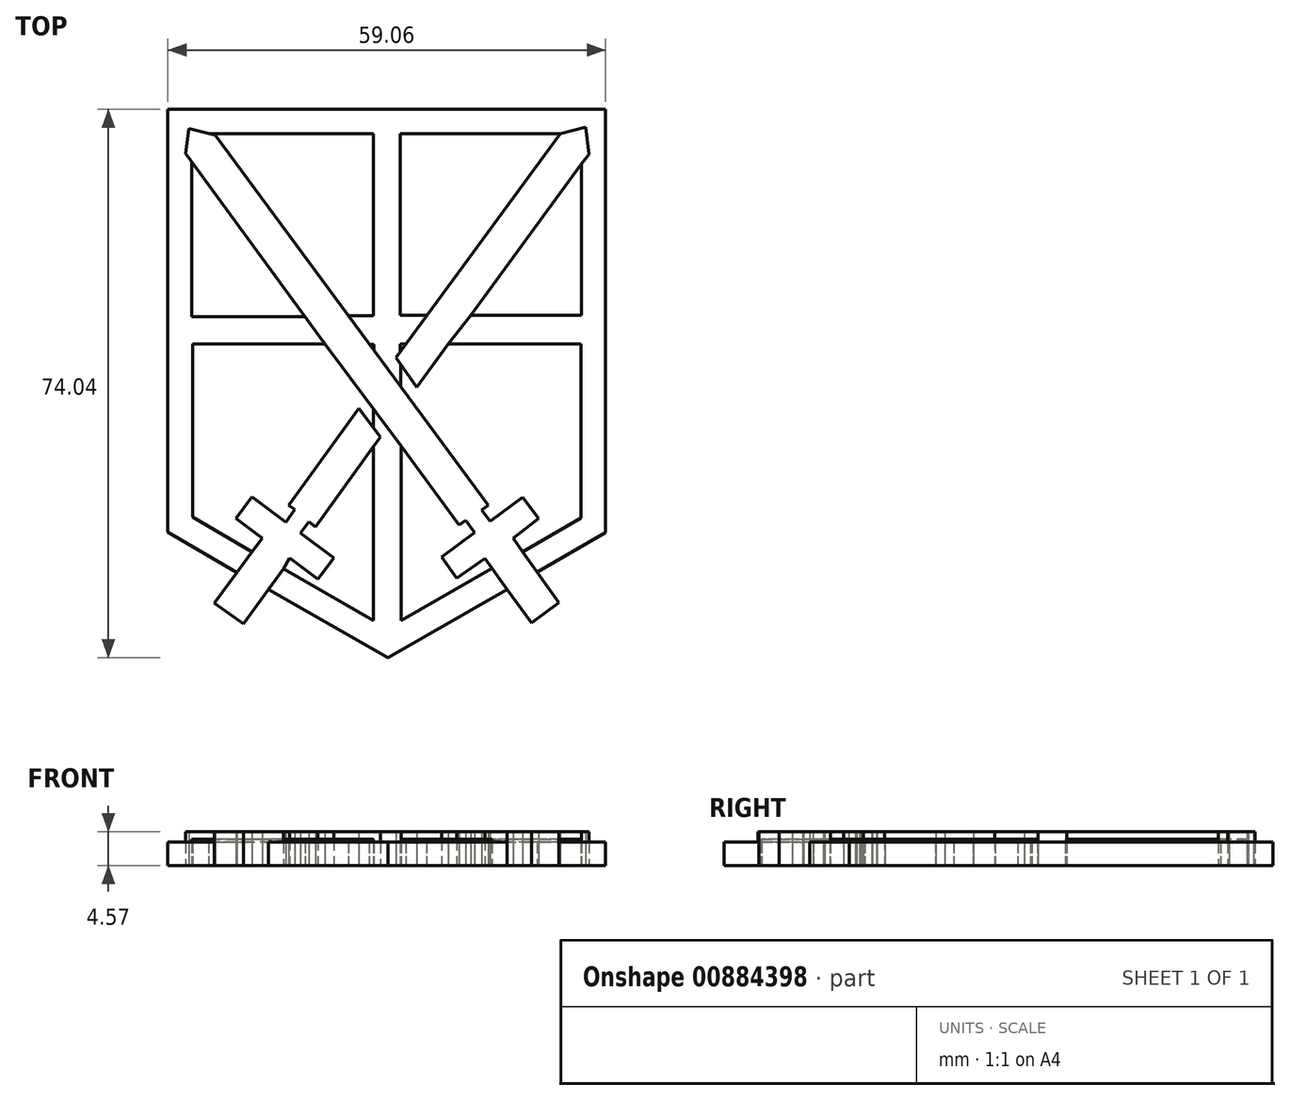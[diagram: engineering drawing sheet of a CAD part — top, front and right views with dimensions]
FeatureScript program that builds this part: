
annotation { "Feature Type Name" : "Feature", "Feature Type Description" : "" }
export const myFeature = defineFeature(function(context is Context, id is Id, definition is map)
    precondition{}
    {
        {
            var Q0;
            Q0=qCreatedBy(makeId("Top.planeOp"),FACE);
            var sketch = newSketch(context, id + "F0", { "sketchPlane" : qUnion([Q0])});
            skLineSegment(sketch, "E0", {"start": v(29.58, 29.95) * mm, "end": v(29.58, -27.22) * mm});
            skLineSegment(sketch, "E1", {"start": v(29.58, -27.22) * mm, "end": v(20.36, -32.55) * mm});
            skLineSegment(sketch, "E2", {"start": v(20.36, -32.55) * mm, "end": v(18.4, -29.78) * mm});
            skLineSegment(sketch, "E3", {"start": v(18.4, -29.78) * mm, "end": v(17.1, -28) * mm});
            skLineSegment(sketch, "E4", {"start": v(20.36, -32.55) * mm, "end": v(23.28, -36.68) * mm});
            skLineSegment(sketch, "E5", {"start": v(23.28, -36.68) * mm, "end": v(19.6, -39.39) * mm});
            skLineSegment(sketch, "E6", {"start": v(19.6, -39.39) * mm, "end": v(16.3, -34.9) * mm});
            skLineSegment(sketch, "E7", {"start": v(16.3, -34.9) * mm, "end": v(14.28, -32.03) * mm});
            skLineSegment(sketch, "E8", {"start": v(14.28, -32.03) * mm, "end": v(13.32, -30.68) * mm});
            skLineSegment(sketch, "E9", {"start": v(16.3, -34.9) * mm, "end": v(0.2, -44.09) * mm});
            skLineSegment(sketch, "E10", {"start": v(0.2, -44.09) * mm, "end": v(-15.92, -34.9) * mm});
            skLineSegment(sketch, "E11", {"start": v(-15.92, -34.9) * mm, "end": v(-19.28, -39.55) * mm});
            skLineSegment(sketch, "E12", {"start": v(-19.28, -39.55) * mm, "end": v(-23.19, -36.72) * mm});
            skLineSegment(sketch, "E13", {"start": v(-23.19, -36.72) * mm, "end": v(-20.19, -32.58) * mm});
            skLineSegment(sketch, "E14", {"start": v(-20.19, -32.58) * mm, "end": v(-18.12, -29.83) * mm});
            skLineSegment(sketch, "E15", {"start": v(-18.12, -29.83) * mm, "end": v(-16.72, -27.98) * mm});
            skLineSegment(sketch, "E16", {"start": v(-16.72, -27.98) * mm, "end": v(-20.3, -25.28) * mm});
            skLineSegment(sketch, "E17", {"start": v(-20.3, -25.28) * mm, "end": v(-18.12, -22.4) * mm});
            skLineSegment(sketch, "E18", {"start": v(-15.92, -34.9) * mm, "end": v(-13.9, -32.13) * mm});
            skLineSegment(sketch, "E19", {"start": v(-13.9, -32.13) * mm, "end": v(-13.05, -30.63) * mm});
            skLineSegment(sketch, "E20", {"start": v(-13.05, -30.63) * mm, "end": v(-9.23, -33.5) * mm});
            skLineSegment(sketch, "E21", {"start": v(-9.23, -33.5) * mm, "end": v(-7.07, -30.63) * mm});
            skLineSegment(sketch, "E22", {"start": v(-13.9, -32.13) * mm, "end": v(-1.74, -39.06) * mm});
            skLineSegment(sketch, "E23", {"start": v(-1.74, -39.06) * mm, "end": v(-1.74, -15.6) * mm});
            skLineSegment(sketch, "E24", {"start": v(13.32, -30.68) * mm, "end": v(9.49, -33.4) * mm});
            skLineSegment(sketch, "E25", {"start": v(9.49, -33.4) * mm, "end": v(7.45, -30.51) * mm});
            skLineSegment(sketch, "E26", {"start": v(7.45, -30.51) * mm, "end": v(18.41, -22.43) * mm});
            skLineSegment(sketch, "E27", {"start": v(18.41, -22.43) * mm, "end": v(20.53, -25.3) * mm});
            skLineSegment(sketch, "E28", {"start": v(20.53, -25.3) * mm, "end": v(17.1, -28) * mm});
            skLineSegment(sketch, "E29", {"start": v(-7.07, -30.63) * mm, "end": v(-18.12, -22.4) * mm});
            skLineSegment(sketch, "E30", {"start": v(2.02, -15.53) * mm, "end": v(2.02, -39.07) * mm});
            skLineSegment(sketch, "E31", {"start": v(2.02, -39.07) * mm, "end": v(14.28, -32.03) * mm});
            skLineSegment(sketch, "E32", {"start": v(18.4, -29.78) * mm, "end": v(26.27, -25.2) * mm});
            skLineSegment(sketch, "E33", {"start": v(26.27, -25.2) * mm, "end": v(26.27, -1.77) * mm});
            skLineSegment(sketch, "E34", {"start": v(26.27, -1.77) * mm, "end": v(8.38, -1.77) * mm});
            skLineSegment(sketch, "E35", {"start": v(8.38, -1.77) * mm, "end": v(11.37, 2.12) * mm});
            skLineSegment(sketch, "E36", {"start": v(11.37, 2.12) * mm, "end": v(26.33, 2.12) * mm});
            skLineSegment(sketch, "E37", {"start": v(26.33, 2.12) * mm, "end": v(26.33, 22.57) * mm});
            skLineSegment(sketch, "E38", {"start": v(26.33, 22.57) * mm, "end": v(27.34, 23.84) * mm});
            skLineSegment(sketch, "E39", {"start": v(27.34, 23.84) * mm, "end": v(26.92, 27.54) * mm});
            skLineSegment(sketch, "E40", {"start": v(26.92, 27.54) * mm, "end": v(23.46, 26.65) * mm});
            skLineSegment(sketch, "E41", {"start": v(23.46, 26.65) * mm, "end": v(1.27, -3.57) * mm});
            skLineSegment(sketch, "E42", {"start": v(1.27, -3.57) * mm, "end": v(4.1, -7.57) * mm});
            skLineSegment(sketch, "E43", {"start": v(4.1, -7.57) * mm, "end": v(8.38, -1.77) * mm});
            skLineSegment(sketch, "E44", {"start": v(11.37, 2.12) * mm, "end": v(26.33, 22.57) * mm});
            skLineSegment(sketch, "E45", {"start": v(23.46, 26.65) * mm, "end": v(1.9, 26.65) * mm});
            skLineSegment(sketch, "E46", {"start": v(1.9, 26.65) * mm, "end": v(1.9, 2.12) * mm});
            skLineSegment(sketch, "E47", {"start": v(1.9, 2.12) * mm, "end": v(5.45, 2.12) * mm});
            skLineSegment(sketch, "E48", {"start": v(29.58, 29.95) * mm, "end": v(-29.48, 29.95) * mm});
            skLineSegment(sketch, "E49", {"start": v(-29.48, 29.95) * mm, "end": v(-29.48, -27.13) * mm});
            skLineSegment(sketch, "E50", {"start": v(-29.48, -27.13) * mm, "end": v(-20.19, -32.58) * mm});
            skLineSegment(sketch, "E51", {"start": v(-18.12, -29.83) * mm, "end": v(-26.13, -25.13) * mm});
            skLineSegment(sketch, "E52", {"start": v(-26.13, -25.13) * mm, "end": v(-26.13, -1.77) * mm});
            skLineSegment(sketch, "E53", {"start": v(-26.13, -1.77) * mm, "end": v(-8.27, -1.77) * mm});
            skLineSegment(sketch, "E54", {"start": v(-8.27, -1.77) * mm, "end": v(2.02, -15.53) * mm});
            skLineSegment(sketch, "E55", {"start": v(2.02, -15.53) * mm, "end": v(9.8, -26.18) * mm});
            skLineSegment(sketch, "E56", {"start": v(9.8, -26.18) * mm, "end": v(10.67, -25.54) * mm});
            skLineSegment(sketch, "E57", {"start": v(10.67, -25.54) * mm, "end": v(11.9, -27.23) * mm});
            skLineSegment(sketch, "E58", {"start": v(14, -25.68) * mm, "end": v(12.87, -24.15) * mm});
            skLineSegment(sketch, "E59", {"start": v(12.87, -24.15) * mm, "end": v(13.74, -23.51) * mm});
            skLineSegment(sketch, "E60", {"start": v(13.74, -23.51) * mm, "end": v(-23.1, 26.43) * mm});
            skLineSegment(sketch, "E61", {"start": v(-23.1, 26.43) * mm, "end": v(-26.62, 27.36) * mm});
            skLineSegment(sketch, "E62", {"start": v(-26.62, 27.36) * mm, "end": v(-27.07, 24) * mm});
            skLineSegment(sketch, "E63", {"start": v(-27.07, 24) * mm, "end": v(-8.27, -1.77) * mm});
            skLineSegment(sketch, "E64", {"start": v(-10.97, 1.92) * mm, "end": v(-26.24, 1.92) * mm});
            skLineSegment(sketch, "E65", {"start": v(-26.24, 1.92) * mm, "end": v(-26.24, 22.87) * mm});
            skLineSegment(sketch, "E66", {"start": v(-1.76, 26.65) * mm, "end": v(-23.96, 26.65) * mm});
            skLineSegment(sketch, "E67", {"start": v(-1.76, 26.65) * mm, "end": v(-1.76, 2.04) * mm});
            skLineSegment(sketch, "E68", {"start": v(-1.76, 2.04) * mm, "end": v(-5.1, 2.04) * mm});
            skLineSegment(sketch, "E69", {"start": v(-1.7, -2.6) * mm, "end": v(-1.7, -1.8) * mm});
            skLineSegment(sketch, "E70", {"start": v(-1.7, -1.8) * mm, "end": v(-2.28, -1.8) * mm});
            skLineSegment(sketch, "E71", {"start": v(1.84, -2.79) * mm, "end": v(1.84, -1.74) * mm});
            skLineSegment(sketch, "E72", {"start": v(1.84, -1.74) * mm, "end": v(2.61, -1.74) * mm});
            skLineSegment(sketch, "E73", {"start": v(1.94, -7.52) * mm, "end": v(1.94, -4.51) * mm});
            skLineSegment(sketch, "E74", {"start": v(-1.72, -10.53) * mm, "end": v(-1.72, -13.1) * mm});
            skLineSegment(sketch, "E75", {"start": v(-1.72, -13.1) * mm, "end": v(-0.81, -14.32) * mm});
            skLineSegment(sketch, "E76", {"start": v(-0.81, -14.32) * mm, "end": v(-1.74, -15.6) * mm});
            skLineSegment(sketch, "E77", {"start": v(-1.72, -13.1) * mm, "end": v(-3.7, -10.45) * mm});
            skLineSegment(sketch, "E78", {"start": v(-3.7, -10.45) * mm, "end": v(-13.16, -23.5) * mm});
            skLineSegment(sketch, "E79", {"start": v(-13.16, -23.5) * mm, "end": v(-12.33, -24.1) * mm});
            skLineSegment(sketch, "E80", {"start": v(-12.33, -24.1) * mm, "end": v(-13.56, -25.8) * mm});
            skLineSegment(sketch, "E81", {"start": v(-11.57, -27.27) * mm, "end": v(-10.45, -25.76) * mm});
            skLineSegment(sketch, "E82", {"start": v(-10.45, -25.76) * mm, "end": v(-9.57, -26.42) * mm});
            skLineSegment(sketch, "E83", {"start": v(-9.57, -26.42) * mm, "end": v(-1.74, -15.6) * mm});
            skSolve(sketch);
        }
        {
            var Q0;
            Q0=makeQuery(id+"F0.imprint","IMPRINT",FACE,{"disambiguationData":[TD([[makeQuery(id+"F0.imprint","IMPRINT",EDGE,{"derivedFrom":sQuery(id+"F0.wireOp",EDGE,"E0")}),-1.0]])]});
            var Q1;
            Q1=makeQuery(id+"F0.imprint","IMPRINT",FACE,{"disambiguationData":[TD([[makeQuery(id+"F0.imprint","IMPRINT",EDGE,{"derivedFrom":sQuery(id+"F0.wireOp",EDGE,"E7")}),1.0]])]});
            extrude(context, id + "F1", {"entities" : qUnion([Q0, Q1]), "depth" : 3.17 * mm, "offsetDistance" : 25.4 * mm});
        }
        {
            var Q0;
            Q0=makeQuery(id+"F0.imprint","IMPRINT",FACE,{"disambiguationData":[TD([[makeQuery(id+"F0.imprint","IMPRINT",EDGE,{"derivedFrom":sQuery(id+"F0.wireOp",EDGE,"E15")}),1.0]])]});
            var Q1;
            {var subQ0=sQuery(id+"F0.wireOp",EDGE,"E64");Q1=makeQuery(id+"F0.imprint","IMPRINT",FACE,{"disambiguationData":[TD([[makeQuery(id+"F0.imprint","IMPRINT",EDGE,{"derivedFrom":subQ0}),-1.0]])]});}
            var Q2;
            {var subQ0=sQuery(id+"F0.wireOp",EDGE,"E66");Q2=makeQuery(id+"F0.imprint","IMPRINT",FACE,{"disambiguationData":[TD([[makeQuery(id+"F0.imprint","IMPRINT",EDGE,{"derivedFrom":subQ0}),1.0]])]});}
            var Q3;
            {var subQ0=sQuery(id+"F0.wireOp",EDGE,"E45");Q3=makeQuery(id+"F0.imprint","IMPRINT",FACE,{"disambiguationData":[TD([[makeQuery(id+"F0.imprint","IMPRINT",EDGE,{"derivedFrom":subQ0}),1.0]])]});}
            var Q4;
            Q4=makeQuery(id+"F0.imprint","IMPRINT",FACE,{"disambiguationData":[TD([[makeQuery(id+"F0.imprint","IMPRINT",EDGE,{"derivedFrom":sQuery(id+"F0.wireOp",EDGE,"E36")}),1.0]])]});
            var Q5;
            Q5=makeQuery(id+"F0.imprint","IMPRINT",FACE,{"disambiguationData":[TD([[makeQuery(id+"F0.imprint","IMPRINT",EDGE,{"derivedFrom":sQuery(id+"F0.wireOp",EDGE,"E3")}),-1.0]])]});
            var Q6;
            Q6=makeQuery(id+"F0.imprint","IMPRINT",FACE,{"disambiguationData":[TD([[makeQuery(id+"F0.imprint","IMPRINT",EDGE,{"derivedFrom":sQuery(id+"F0.wireOp",EDGE,"E8")}),1.0]])]});
            var Q7;
            Q7=makeQuery(id+"F0.imprint","IMPRINT",FACE,{"disambiguationData":[TD([[makeQuery(id+"F0.imprint","IMPRINT",EDGE,{"derivedFrom":sQuery(id+"F0.wireOp",EDGE,"E19")}),-1.0]])]});
            var Q8;
            {var subQ0=sQuery(id+"F0.wireOp",EDGE,"E71");Q8=makeQuery(id+"F0.imprint","IMPRINT",FACE,{"disambiguationData":[TD([[makeQuery(id+"F0.imprint","IMPRINT",EDGE,{"derivedFrom":subQ0}),-1.0]])]});}
            var Q9;
            {var subQ0=sQuery(id+"F0.wireOp",EDGE,"E69");Q9=makeQuery(id+"F0.imprint","IMPRINT",FACE,{"disambiguationData":[TD([[makeQuery(id+"F0.imprint","IMPRINT",EDGE,{"derivedFrom":subQ0}),1.0]])]});}
            extrude(context, id + "F2", {"entities" : qUnion([Q0, Q1, Q2, Q3, Q4, Q5, Q6, Q7, Q8, Q9]), "depth" : 3.56 * mm, "offsetDistance" : 25.4 * mm});
        }
        {
            var Q0;
            {var subQ14=sQuery(id+"F0.wireOp",EDGE,"E55");Q0=makeQuery(id+"F0.imprint","IMPRINT",FACE,{"disambiguationData":[TD([[makeQuery(id+"F0.imprint","IMPRINT",EDGE,{"derivedFrom":subQ14}),1.0]])]});}
            var Q1;
            Q1=makeQuery(id+"F0.imprint","IMPRINT",FACE,{"disambiguationData":[TD([[makeQuery(id+"F0.imprint","IMPRINT",EDGE,{"derivedFrom":sQuery(id+"F0.wireOp",EDGE,"E35")}),1.0]])]});
            var Q2;
            Q2=makeQuery(id+"F0.imprint","IMPRINT",FACE,{"disambiguationData":[TD([[makeQuery(id+"F0.imprint","IMPRINT",EDGE,{"derivedFrom":sQuery(id+"F0.wireOp",EDGE,"E75")}),-1.0]])]});
            var Q3;
            Q3=makeQuery(id+"F0.imprint","IMPRINT",FACE,{"disambiguationData":[TD([[makeQuery(id+"F0.imprint","IMPRINT",EDGE,{"derivedFrom":sQuery(id+"F0.wireOp",EDGE,"E11")}),-1.0]])]});
            var Q4;
            Q4=makeQuery(id+"F0.imprint","IMPRINT",FACE,{"disambiguationData":[TD([[makeQuery(id+"F0.imprint","IMPRINT",EDGE,{"derivedFrom":sQuery(id+"F0.wireOp",EDGE,"E2")}),1.0]])]});
            extrude(context, id + "F3", {"entities" : qUnion([Q0, Q1, Q2, Q3, Q4]), "depth" : 4.57 * mm, "offsetDistance" : 25.4 * mm});
        }
    });
